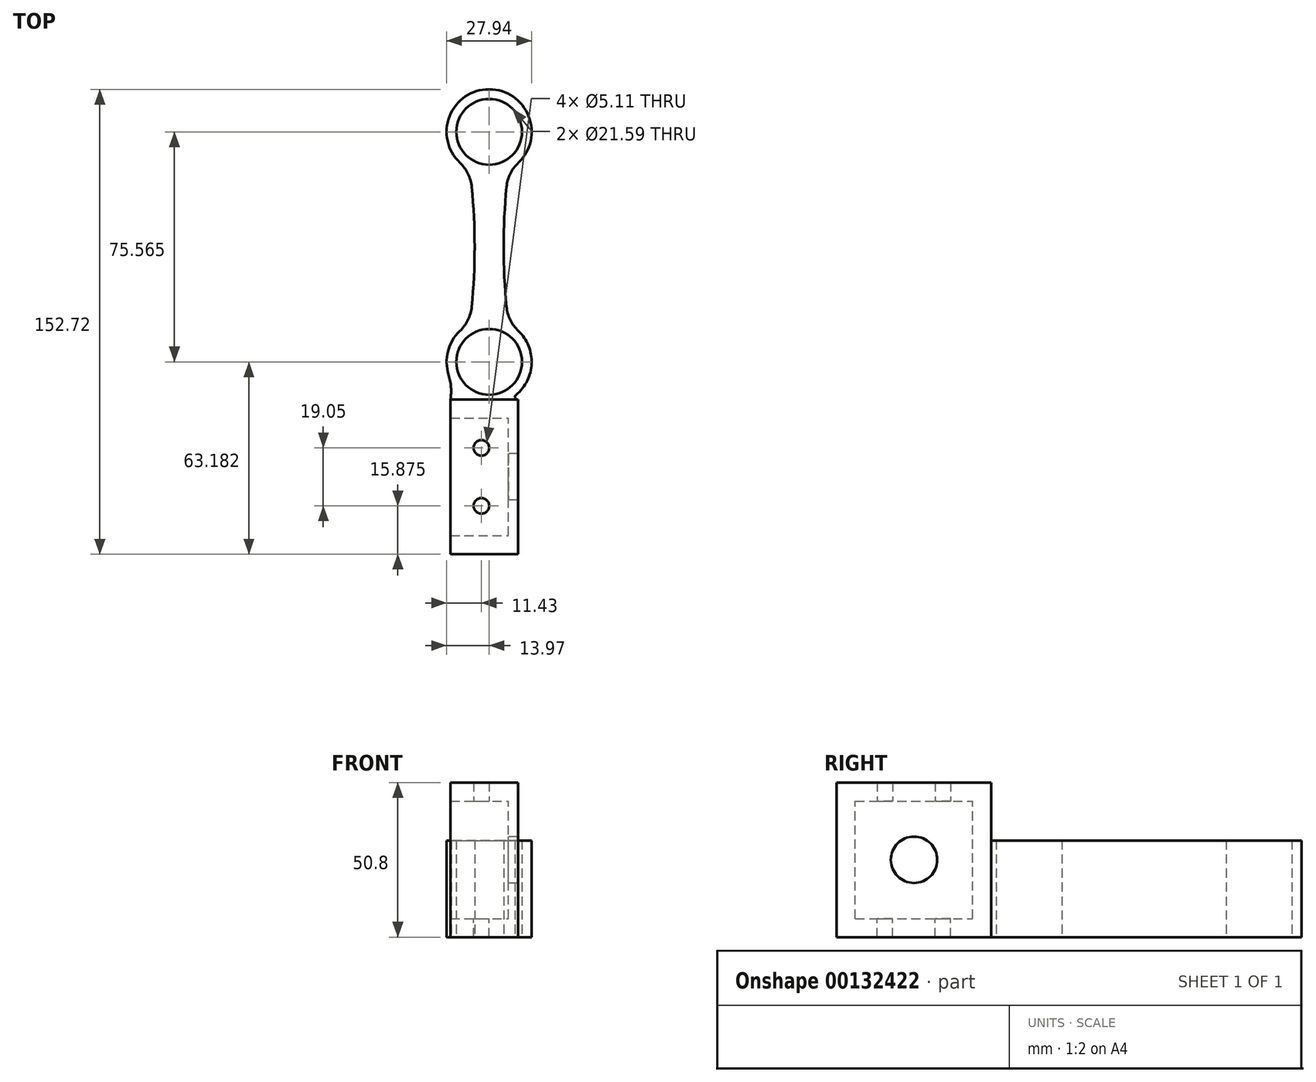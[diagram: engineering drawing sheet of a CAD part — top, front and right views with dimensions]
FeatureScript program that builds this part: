
annotation { "Feature Type Name" : "Feature", "Feature Type Description" : "" }
export const myFeature = defineFeature(function(context is Context, id is Id, definition is map)
    precondition{}
    {
        {
            var Q0;
            Q0=qCreatedBy(makeId("Right.planeOp"),FACE);
            var sketch = newSketch(context, id + "F0", { "sketchPlane" : qUnion([Q0])});
            skLineSegment(sketch, "E0.bottom", {"start": v(0, 0) * mm, "end": v(50.8, 0) * mm});
            skLineSegment(sketch, "E0.top", {"start": v(0, 50.8) * mm, "end": v(50.8, 50.8) * mm});
            skLineSegment(sketch, "E0.left", {"start": v(0, 0) * mm, "end": v(0, 50.8) * mm});
            skLineSegment(sketch, "E0.right", {"start": v(50.8, 0) * mm, "end": v(50.8, 50.8) * mm});
            skLineSegment(sketch, "E1.bottom", {"start": v(6.1, 6.1) * mm, "end": v(44.7, 6.1) * mm});
            skLineSegment(sketch, "E1.top", {"start": v(6.1, 44.7) * mm, "end": v(44.7, 44.7) * mm});
            skLineSegment(sketch, "E1.left", {"start": v(6.1, 6.1) * mm, "end": v(6.1, 44.7) * mm});
            skLineSegment(sketch, "E1.right", {"start": v(44.7, 6.1) * mm, "end": v(44.7, 44.7) * mm});
            skCircle(sketch, "E2", {"center": v(25.4, 25.4) * mm, "radius": 7.62 * mm});
            skPoint(sketch, "E2.centerSnap0", {"position": v(6.1, 25.4) * mm});
            skPoint(sketch, "E2.centerSnap1", {"position": v(25.4, 6.1) * mm});
            skSolve(sketch);
        }
        {
            var Q0;
            Q0=makeQuery(id+"F0.imprint","IMPRINT",FACE,{"disambiguationData":[TD([[makeQuery(id+"F0.imprint","IMPRINT",EDGE,{"derivedFrom":sQuery(id+"F0.wireOp",EDGE,"E0.bottom")}),1.0]])]});
            extrude(context, id + "F1", {"entities" : qUnion([Q0]), "oppositeDirection" : true, "depth" : 12.7 * mm});
        }
        {
            var Q0;
            Q0=makeQuery(id+"F0.imprint","IMPRINT",FACE,{"disambiguationData":[TD([[makeQuery(id+"F0.imprint","IMPRINT",EDGE,{"derivedFrom":sQuery(id+"F0.wireOp",EDGE,"E1.bottom")}),1.0]])]});
            var Q1;
            Q1=makeQuery(id+"F0.imprint","IMPRINT",FACE,{"disambiguationData":[TD([[makeQuery(id+"F0.imprint","IMPRINT",EDGE,{"derivedFrom":sQuery(id+"F0.wireOp",EDGE,"E0.bottom")}),1.0]])]});
            extrude(context, id + "F2", {"entities" : qUnion([Q0, Q1]), "operationType" : NewBodyOperationType.ADD, "depth" : 3.17 * mm});
        }
        {
            var Q0;
            Q0=makeQuery(id+"F1.opExtrude","SWEPT_FACE",FACE,{"disambiguationData":[OSD([sQuery(id+"F0.wireOp",EDGE,"E1.top")])]});
            var sketch = newSketch(context, id + "F3", { "sketchPlane" : qUnion([Q0])});
            skLineSegment(sketch, "E3.0.0", {"start": v(0, -44.7) * mm, "end": v(0, -6.1) * mm});
            skLineSegment(sketch, "E3.0.1", {"start": v(0, -6.1) * mm, "end": v(-12.7, -6.1) * mm});
            skLineSegment(sketch, "E3.0.2", {"start": v(-12.7, -6.1) * mm, "end": v(-12.7, -44.7) * mm});
            skLineSegment(sketch, "E3.0.3", {"start": v(-12.7, -44.7) * mm, "end": v(0, -44.7) * mm});
            skPoint(sketch, "E4", {"position": v(-8.9, -34.92) * mm});
            skPoint(sketch, "E5", {"position": v(-8.9, -15.87) * mm});
            skPoint(sketch, "E6", {"position": v(-12.7, -25.4) * mm});
            skSolve(sketch);
        }
        {
            var Q0;
            Q0=sQuery(id+"F3.wireOp",VERTEX,"E5");
            var Q1;
            Q1=sQuery(id+"F3.wireOp",VERTEX,"E4");
            var Q2;
            Q2=makeQuery(id+"F1.opExtrude","SWEPT_BODY",BODY,{"disambiguationData":[OSD([sQuery(id+"F0.wireOp",EDGE,"E0.bottom"),sQuery(id+"F0.wireOp",EDGE,"E0.top"),sQuery(id+"F0.wireOp",EDGE,"E0.left"),sQuery(id+"F0.wireOp",EDGE,"E0.right"),sQuery(id+"F0.wireOp",EDGE,"E1.bottom"),sQuery(id+"F0.wireOp",EDGE,"E1.top"),sQuery(id+"F0.wireOp",EDGE,"E1.left"),sQuery(id+"F0.wireOp",EDGE,"E1.right")])]});
            hole(context, id + "F4", {"style" : HoleStyle.SIMPLE, "endStyle" : HoleEndStyle.THROUGH, "standardTappedOrClearance" : lookupTablePath({ "standard" : "ANSI", "fit" : "Normal (ASME)", "size" : "#10", "type" : "Clearance" }), "standardBlindInLast" : lookupTablePath({ "fit" : "Free", "standard" : "ANSI", "size" : "#10", "type" : "Clearance" }), "holeDiameter" : 5.1 * mm, "locations" : qUnion([Q0, Q1]), "scope" : qUnion([Q2]), "isTappedThrough" : true});
        }
        {
            var Q0;
            Q0=makeQuery(id+"F1.opExtrude","SWEPT_FACE",FACE,{"disambiguationData":[OSD([sQuery(id+"F0.wireOp",EDGE,"E1.top")])]});
            var sketch = newSketch(context, id + "F5", { "sketchPlane" : qUnion([Q0])});
            skCircle(sketch, "E7.0", {"center": v(-8.9, -15.87) * mm, "radius": 2.55 * mm});
            skCircle(sketch, "E8.0", {"center": v(-8.9, -34.92) * mm, "radius": 2.55 * mm});
            skSolve(sketch);
        }
        {
            var Q0;
            Q0=makeQuery(id+"F5.imprint","IMPRINT",FACE,{"disambiguationData":[TD([[makeQuery(id+"F5.imprint","IMPRINT",EDGE,{"derivedFrom":sQuery(id+"F5.wireOp",EDGE,"E7.0")}),1.0]])]});
            var Q1;
            Q1=makeQuery(id+"F5.imprint","IMPRINT",FACE,{"disambiguationData":[TD([[makeQuery(id+"F5.imprint","IMPRINT",EDGE,{"derivedFrom":sQuery(id+"F5.wireOp",EDGE,"E8.0")}),1.0]])]});
            extrude(context, id + "F6", {"entities" : qUnion([Q0, Q1]), "operationType" : NewBodyOperationType.REMOVE, "depth" : 82.82 * mm});
        }
        {
            var Q0;
            Q0=makeQuery(id+"F1.opExtrude","CAP_FACE",FACE,{"disambiguationData":[OSD([sQuery(id+"F0.wireOp",EDGE,"E0.bottom"),sQuery(id+"F0.wireOp",EDGE,"E0.top"),sQuery(id+"F0.wireOp",EDGE,"E0.left"),sQuery(id+"F0.wireOp",EDGE,"E0.right"),sQuery(id+"F0.wireOp",EDGE,"E1.bottom"),sQuery(id+"F0.wireOp",EDGE,"E1.top"),sQuery(id+"F0.wireOp",EDGE,"E1.left"),sQuery(id+"F0.wireOp",EDGE,"E1.right")])],"isStart":false});
            extrude(context, id + "F7", {"entities" : qUnion([Q0]), "operationType" : NewBodyOperationType.ADD, "depth" : 6.35 * mm});
        }
        {
            var Q0;
            {var subQ0=sQuery(id+"F0.wireOp",EDGE,"E0.bottom");Q0=makeQuery(id+"F7.boolean.opBoolean","MERGE",FACE,{"derivedFrom":[makeQuery(id+"F2.boolean.opBoolean","MERGE",FACE,{"derivedFrom":[makeQuery(id+"F1.opExtrude","SWEPT_FACE",FACE,{"disambiguationData":[OSD([subQ0])]}),makeQuery(id+"F2.opExtrude","SWEPT_FACE",FACE,{"disambiguationData":[OSD([subQ0])]})]}),makeQuery(id+"F7.opExtrude","SWEPT_FACE",FACE,{"disambiguationData":[OSD([subQ0])]})]});}
            var sketch = newSketch(context, id + "F8", { "sketchPlane" : qUnion([Q0])});
            skLineSegment(sketch, "E9.0.0", {"start": v(-19.05, -50.8) * mm, "end": v(3.17, -50.8) * mm});
            skLineSegment(sketch, "E9.0.1", {"start": v(3.18, -50.8) * mm, "end": v(3.18, 0) * mm});
            skLineSegment(sketch, "E9.0.2", {"start": v(3.17, 0) * mm, "end": v(-19.05, 0) * mm});
            skLineSegment(sketch, "E9.0.3", {"start": v(-19.05, 0) * mm, "end": v(-19.05, -50.8) * mm});
            skCircle(sketch, "E10", {"center": v(-6.35, -138.75) * mm, "radius": 13.97 * mm});
            skCircle(sketch, "E11", {"center": v(-6.35, -63.18) * mm, "radius": 13.97 * mm});
            skCircle(sketch, "E12", {"center": v(-6.35, -138.75) * mm, "radius": 10.8 * mm});
            skCircle(sketch, "E13", {"center": v(-6.35, -63.18) * mm, "radius": 10.8 * mm});
            skPoint(sketch, "E14", {"position": v(3.17, -25.4) * mm});
            skPoint(sketch, "E15", {"position": v(-6.29, -25.4) * mm});
            skLineSegment(sketch, "E16", {"start": v(3.17, -25.4) * mm, "end": v(-6.29, -25.4) * mm, "construction": true});
            skPoint(sketch, "E17", {"position": v(-6.35, -124.78) * mm});
            skPoint(sketch, "E18", {"position": v(-6.35, -77.15) * mm});
            skLineSegment(sketch, "E19", {"start": v(-6.35, -124.78) * mm, "end": v(3.17, -124.78) * mm, "construction": true});
            skLineSegment(sketch, "E20", {"start": v(-6.35, -77.15) * mm, "end": v(3.17, -77.15) * mm, "construction": true});
            skLineSegment(sketch, "E21.bottom", {"start": v(0, -75.63) * mm, "end": v(-12.7, -75.63) * mm});
            skLineSegment(sketch, "E21.top", {"start": v(0, -126.3) * mm, "end": v(-12.7, -126.3) * mm});
            skLineSegment(sketch, "E21.left", {"start": v(0, -75.63) * mm, "end": v(0, -126.3) * mm, "construction": true});
            skLineSegment(sketch, "E21.right", {"start": v(-12.7, -75.63) * mm, "end": v(-12.7, -126.3) * mm, "construction": true});
            skArc(sketch, "E22", {"start": v(0, -75.63) * mm, "mid": v(-1.59, -100.97) * mm, "end": v(0, -126.3) * mm});
            skArc(sketch, "E23", {"start": v(-12.7, -126.3) * mm, "mid": v(-11.11, -100.97) * mm, "end": v(-12.7, -75.63) * mm});
            skSolve(sketch);
        }
        {
            var Q0;
            {var subQ3=sQuery(id+"F8.wireOp",EDGE,"E13");Q0=makeQuery(id+"F8.imprint","IMPRINT",FACE,{"disambiguationData":[TD([[makeQuery(id+"F8.imprint","IMPRINT",EDGE,{"derivedFrom":subQ3}),-1.0]])]});}
            var Q1;
            {var subQ0=sQuery(id+"F8.wireOp",EDGE,"E11");var subQ1=sQuery(id+"F8.wireOp",EDGE,"E9.0.0");var subQ2=makeQuery(id+"F8.imprint","INTERSECT",VERTEX,{"disambiguationData":[OD(0.0)],"derivedFrom":[subQ1,subQ0]});Q1=makeQuery(id+"F8.imprint","IMPRINT",FACE,{"disambiguationData":[TD([[makeQuery(id+"F8.imprint","IMPRINT",EDGE,{"disambiguationData":[TD([[subQ2,-1.0]])],"derivedFrom":subQ1}),1.0]])]});}
            var Q2;
            {var subQ0=sQuery(id+"F8.wireOp",EDGE,"E22");Q2=makeQuery(id+"F8.imprint","IMPRINT",FACE,{"disambiguationData":[TD([[makeQuery(id+"F8.imprint","IMPRINT",EDGE,{"derivedFrom":subQ0}),-1.0]])]});}
            var Q3;
            Q3=makeQuery(id+"F8.imprint","IMPRINT",FACE,{"disambiguationData":[TD([[makeQuery(id+"F8.imprint","IMPRINT",EDGE,{"derivedFrom":sQuery(id+"F8.wireOp",EDGE,"E12")}),-1.0]])]});
            var Q4;
            {var subQ0=sQuery(id+"F8.wireOp",EDGE,"E21.top");Q4=makeQuery(id+"F8.imprint","IMPRINT",FACE,{"disambiguationData":[TD([[makeQuery(id+"F8.imprint","IMPRINT",EDGE,{"derivedFrom":subQ0}),-1.0]])]});}
            var Q5;
            {var subQ0=sQuery(id+"F8.wireOp",EDGE,"E21.bottom");Q5=makeQuery(id+"F8.imprint","IMPRINT",FACE,{"disambiguationData":[TD([[makeQuery(id+"F8.imprint","IMPRINT",EDGE,{"derivedFrom":subQ0}),1.0]])]});}
            var Q6;
            {var subQ0=sQuery(id+"F0.wireOp",EDGE,"E0.top");Q6=makeQuery(id+"F7.boolean.opBoolean","MERGE",FACE,{"derivedFrom":[makeQuery(id+"F2.boolean.opBoolean","MERGE",FACE,{"derivedFrom":[makeQuery(id+"F1.opExtrude","SWEPT_FACE",FACE,{"disambiguationData":[OSD([subQ0])]}),makeQuery(id+"F2.opExtrude","SWEPT_FACE",FACE,{"disambiguationData":[OSD([subQ0])]})]}),makeQuery(id+"F7.opExtrude","SWEPT_FACE",FACE,{"disambiguationData":[OSD([subQ0])]})]});}
            extrude(context, id + "F9", {"entities" : qUnion([Q0, Q1, Q2, Q3, Q4, Q5]), "operationType" : NewBodyOperationType.ADD, "oppositeDirection" : true, "endBoundEntityFace" : qUnion([Q6]), "depth" : 31.75 * mm});
        }
        {
            var Q0;
            {var subQ0=sQuery(id+"F0.wireOp",EDGE,"E0.right");Q0=makeQuery(id+"F9.boolean.opBoolean","INTERSECT",EDGE,{"disambiguationData":[OD(0.0)],"derivedFrom":[makeQuery(id+"F7.boolean.opBoolean","MERGE",FACE,{"derivedFrom":[makeQuery(id+"F2.boolean.opBoolean","MERGE",FACE,{"derivedFrom":[makeQuery(id+"F1.opExtrude","SWEPT_FACE",FACE,{"disambiguationData":[OSD([subQ0])]}),makeQuery(id+"F2.opExtrude","SWEPT_FACE",FACE,{"disambiguationData":[OSD([subQ0])]})]}),makeQuery(id+"F7.opExtrude","SWEPT_FACE",FACE,{"disambiguationData":[OSD([subQ0])]})]}),makeQuery(id+"F9.opExtrude","SWEPT_FACE",FACE,{"disambiguationData":[OSD([sQuery(id+"F8.wireOp",EDGE,"E11")])]})]});}
            var Q1;
            {var subQ0=sQuery(id+"F0.wireOp",EDGE,"E0.left");Q1=makeQuery(id+"F9.boolean.opBoolean","INTERSECT",EDGE,{"disambiguationData":[OD(0.0)],"derivedFrom":[makeQuery(id+"F7.boolean.opBoolean","MERGE",FACE,{"derivedFrom":[makeQuery(id+"F2.boolean.opBoolean","MERGE",FACE,{"derivedFrom":[makeQuery(id+"F1.opExtrude","SWEPT_FACE",FACE,{"disambiguationData":[OSD([subQ0])]}),makeQuery(id+"F2.opExtrude","SWEPT_FACE",FACE,{"disambiguationData":[OSD([subQ0])]})]}),makeQuery(id+"F7.opExtrude","SWEPT_FACE",FACE,{"disambiguationData":[OSD([subQ0])]})]}),makeQuery(id+"F9.opExtrude","SWEPT_FACE",FACE,{"disambiguationData":[OSD([sQuery(id+"F8.wireOp",EDGE,"E10")])]})]});}
            fillet(context, id + "F10", {"entities" : qUnion([Q0, Q1]), "radius" : 0.89 * mm, "tangentPropagation" : true, "allowEdgeOverflow" : false});
        }
        {
            var Q0;
            {var subQ0=sQuery(id+"F0.wireOp",EDGE,"E0.right");Q0=makeQuery(id+"F9.boolean.opBoolean","INTERSECT",EDGE,{"disambiguationData":[OD(1.0)],"derivedFrom":[makeQuery(id+"F7.boolean.opBoolean","MERGE",FACE,{"derivedFrom":[makeQuery(id+"F2.boolean.opBoolean","MERGE",FACE,{"derivedFrom":[makeQuery(id+"F1.opExtrude","SWEPT_FACE",FACE,{"disambiguationData":[OSD([subQ0])]}),makeQuery(id+"F2.opExtrude","SWEPT_FACE",FACE,{"disambiguationData":[OSD([subQ0])]})]}),makeQuery(id+"F7.opExtrude","SWEPT_FACE",FACE,{"disambiguationData":[OSD([subQ0])]})]}),makeQuery(id+"F9.opExtrude","SWEPT_FACE",FACE,{"disambiguationData":[OSD([sQuery(id+"F8.wireOp",EDGE,"E11")])]})]});}
            var Q1;
            {var subQ0=sQuery(id+"F0.wireOp",EDGE,"E0.left");Q1=makeQuery(id+"F9.boolean.opBoolean","INTERSECT",EDGE,{"disambiguationData":[OD(1.0)],"derivedFrom":[makeQuery(id+"F7.boolean.opBoolean","MERGE",FACE,{"derivedFrom":[makeQuery(id+"F2.boolean.opBoolean","MERGE",FACE,{"derivedFrom":[makeQuery(id+"F1.opExtrude","SWEPT_FACE",FACE,{"disambiguationData":[OSD([subQ0])]}),makeQuery(id+"F2.opExtrude","SWEPT_FACE",FACE,{"disambiguationData":[OSD([subQ0])]})]}),makeQuery(id+"F7.opExtrude","SWEPT_FACE",FACE,{"disambiguationData":[OSD([subQ0])]})]}),makeQuery(id+"F9.opExtrude","SWEPT_FACE",FACE,{"disambiguationData":[OSD([sQuery(id+"F8.wireOp",EDGE,"E10")])]})]});}
            fillet(context, id + "F11", {"entities" : qUnion([Q0, Q1]), "radius" : 17.78 * mm, "tangentPropagation" : true, "allowEdgeOverflow" : false});
        }
        {
            var Q0;
            Q0=makeQuery(id+"F9.opExtrude","SWEPT_EDGE",EDGE,{"disambiguationData":[OSD([sQuery(id+"F8.wireOp",EDGE,"E11"),sQuery(id+"F8.wireOp",EDGE,"E21.bottom"),sQuery(id+"F8.wireOp",EDGE,"E23")])]});
            var Q1;
            Q1=makeQuery(id+"F9.opExtrude","SWEPT_EDGE",EDGE,{"disambiguationData":[OSD([sQuery(id+"F8.wireOp",EDGE,"E10"),sQuery(id+"F8.wireOp",EDGE,"E21.top"),sQuery(id+"F8.wireOp",EDGE,"E23")])]});
            var Q2;
            Q2=makeQuery(id+"F9.opExtrude","SWEPT_EDGE",EDGE,{"disambiguationData":[OSD([sQuery(id+"F8.wireOp",EDGE,"E11"),sQuery(id+"F8.wireOp",EDGE,"E21.bottom"),sQuery(id+"F8.wireOp",EDGE,"E22")])]});
            var Q3;
            Q3=makeQuery(id+"F9.opExtrude","SWEPT_EDGE",EDGE,{"disambiguationData":[OSD([sQuery(id+"F8.wireOp",EDGE,"E10"),sQuery(id+"F8.wireOp",EDGE,"E21.top"),sQuery(id+"F8.wireOp",EDGE,"E22")])]});
            fillet(context, id + "F12", {"entities" : qUnion([Q0, Q1, Q2, Q3]), "radius" : 12.7 * mm, "tangentPropagation" : true, "allowEdgeOverflow" : false});
        }
    });
